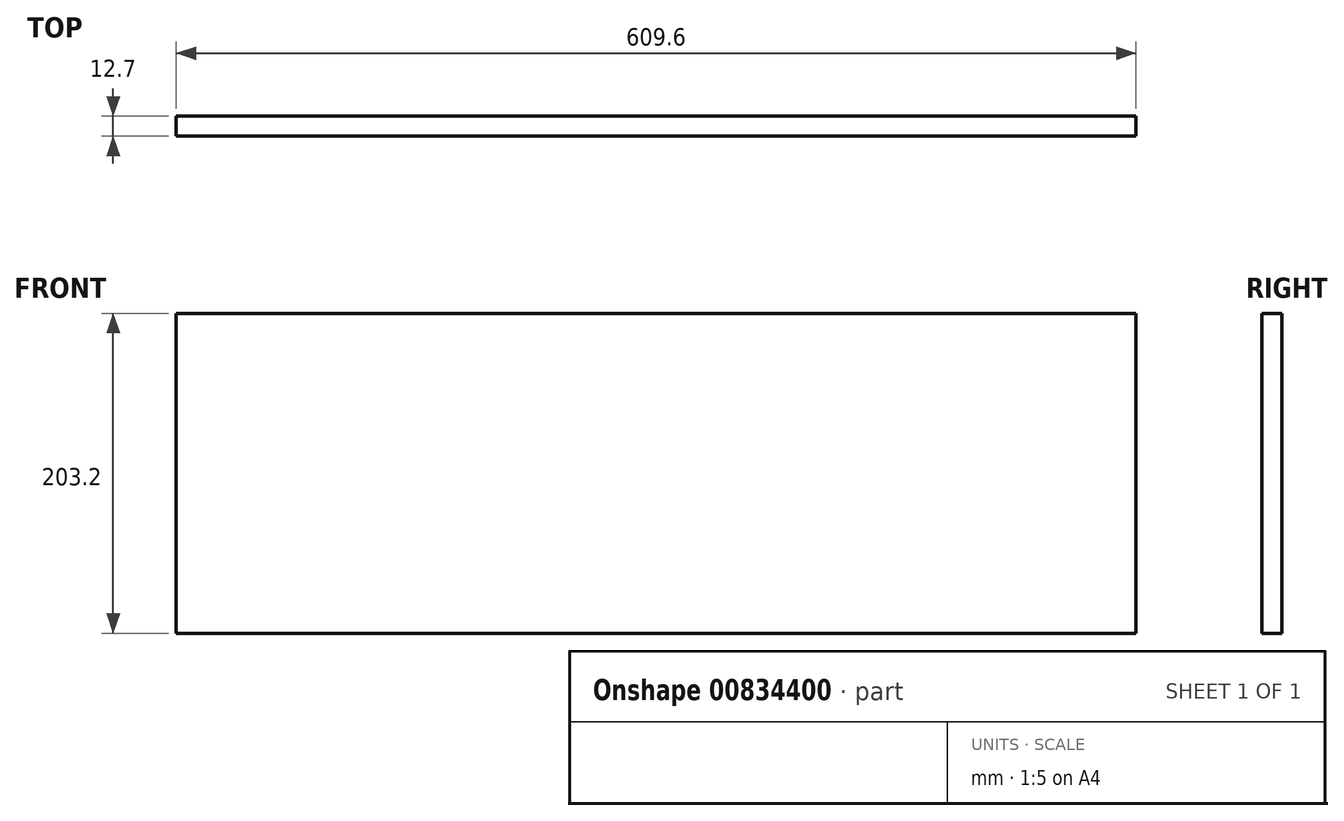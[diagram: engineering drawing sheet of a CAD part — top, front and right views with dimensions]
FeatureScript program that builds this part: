
annotation { "Feature Type Name" : "Feature", "Feature Type Description" : "" }
export const myFeature = defineFeature(function(context is Context, id is Id, definition is map)
    precondition{}
    {
        {
            var Q0;
            Q0=qCreatedBy(makeId("Front.planeOp"),FACE);
            var sketch = newSketch(context, id + "F0", { "sketchPlane" : qUnion([Q0])});
            skLineSegment(sketch, "E0.bottom", {"start": v(-298.5, 61.62) * mm, "end": v(311.1, 61.62) * mm});
            skLineSegment(sketch, "E0.top", {"start": v(-298.5, -141.58) * mm, "end": v(311.1, -141.58) * mm});
            skLineSegment(sketch, "E0.left", {"start": v(-298.5, 61.62) * mm, "end": v(-298.5, -141.58) * mm});
            skLineSegment(sketch, "E0.right", {"start": v(311.1, 61.62) * mm, "end": v(311.1, -141.58) * mm});
            skLineSegment(sketch, "E1", {"start": v(-279.02, 61.62) * mm, "end": v(-279.02, -141.58) * mm});
            skLineSegment(sketch, "E2", {"start": v(298.4, 61.62) * mm, "end": v(298.4, -141.58) * mm});
            skSolve(sketch);
        }
        {
            var Q0;
            Q0=makeQuery(id+"F0.imprint","IMPRINT",FACE,{"disambiguationData":[TD([[makeQuery(id+"F0.imprint","IMPRINT",EDGE,{"derivedFrom":sQuery(id+"F0.wireOp",EDGE,"E0.bottom")}),-1.0]])]});
            extrude(context, id + "F1", {"entities" : qUnion([Q0]), "oppositeDirection" : true, "depth" : 12.7 * mm, "offsetDistance" : 25.4 * mm});
        }
    });
